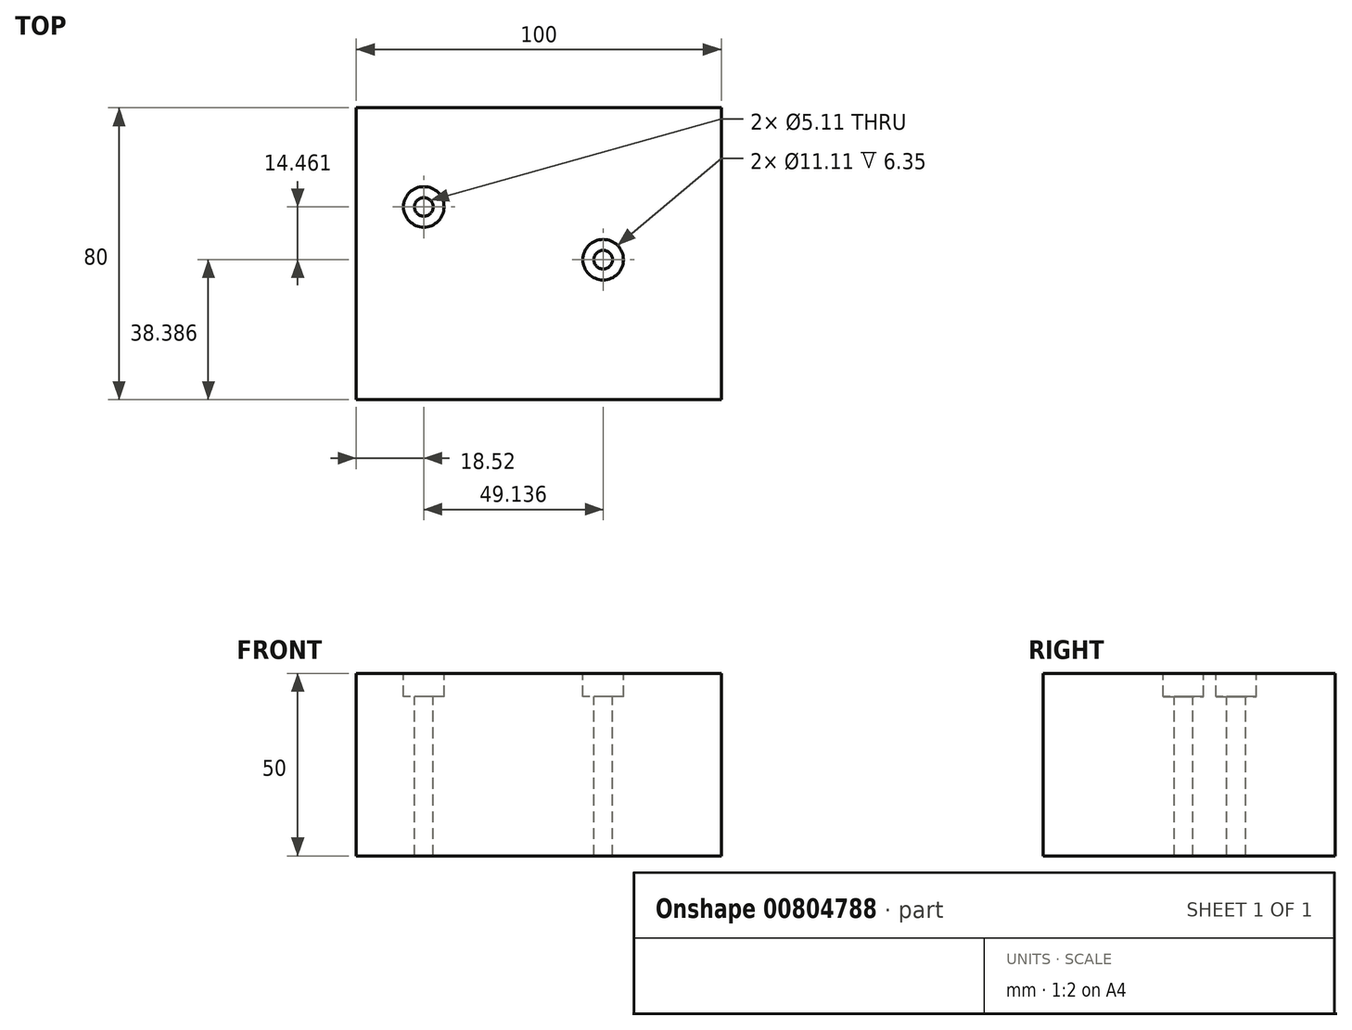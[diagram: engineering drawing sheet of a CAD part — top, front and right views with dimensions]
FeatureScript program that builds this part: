
annotation { "Feature Type Name" : "Feature", "Feature Type Description" : "" }
export const myFeature = defineFeature(function(context is Context, id is Id, definition is map)
    precondition{}
    {
        {
            var Q0;
            Q0=qCreatedBy(makeId("Top.planeOp"),FACE);
            var sketch = newSketch(context, id + "F0", { "sketchPlane" : qUnion([Q0])});
            skLineSegment(sketch, "E0.bottom", {"start": v(-49.53, -15.17) * mm, "end": v(50.47, -15.17) * mm});
            skLineSegment(sketch, "E0.top", {"start": v(-49.53, 64.83) * mm, "end": v(50.47, 64.83) * mm});
            skLineSegment(sketch, "E0.left", {"start": v(-49.53, -15.17) * mm, "end": v(-49.53, 64.83) * mm});
            skLineSegment(sketch, "E0.right", {"start": v(50.47, -15.17) * mm, "end": v(50.47, 64.83) * mm});
            skSolve(sketch);
        }
        {
            var Q0;
            Q0=makeQuery(id+"F0.imprint","IMPRINT",FACE,{"disambiguationData":[TD([[makeQuery(id+"F0.imprint","IMPRINT",EDGE,{"derivedFrom":sQuery(id+"F0.wireOp",EDGE,"E0.bottom")}),1.0]])]});
            extrude(context, id + "F1", {"entities" : qUnion([Q0]), "depth" : 50 * mm, "offsetDistance" : 25 * mm});
        }
        {
            var Q0;
            Q0=makeQuery(id+"F1.opExtrude","CAP_FACE",FACE,{"disambiguationData":[OSD([sQuery(id+"F0.wireOp",EDGE,"E0.bottom"),sQuery(id+"F0.wireOp",EDGE,"E0.top"),sQuery(id+"F0.wireOp",EDGE,"E0.left"),sQuery(id+"F0.wireOp",EDGE,"E0.right")])],"isStart":false});
            var sketch = newSketch(context, id + "F2", { "sketchPlane" : qUnion([Q0])});
            skPoint(sketch, "E1", {"position": v(-31, 37.68) * mm});
            skPoint(sketch, "E2", {"position": v(18.13, 23.22) * mm});
            skSolve(sketch);
        }
        {
            var Q0;
            Q0=sQuery(id+"F2.wireOp",VERTEX,"E1");
            var Q1;
            Q1=sQuery(id+"F2.wireOp",VERTEX,"E2");
            var Q2;
            Q2=makeQuery(id+"F1.opExtrude","SWEPT_BODY",BODY,{"disambiguationData":[OSD([sQuery(id+"F0.wireOp",EDGE,"E0.bottom"),sQuery(id+"F0.wireOp",EDGE,"E0.top"),sQuery(id+"F0.wireOp",EDGE,"E0.left"),sQuery(id+"F0.wireOp",EDGE,"E0.right")])]});
            hole(context, id + "F3", {"style" : HoleStyle.C_BORE, "endStyle" : HoleEndStyle.THROUGH, "holeDiameter" : 5.11 * mm, "cBoreDiameter" : 11.1 * mm, "cBoreDepth" : 6.35 * mm, "majorDiameter" : 5 * mm, "isTappedThrough" : true, "tappedDepth" : 12 * mm, "tapClearance" : 3, "locations" : qUnion([Q0, Q1]), "scope" : qUnion([Q2])});
        }
    });
